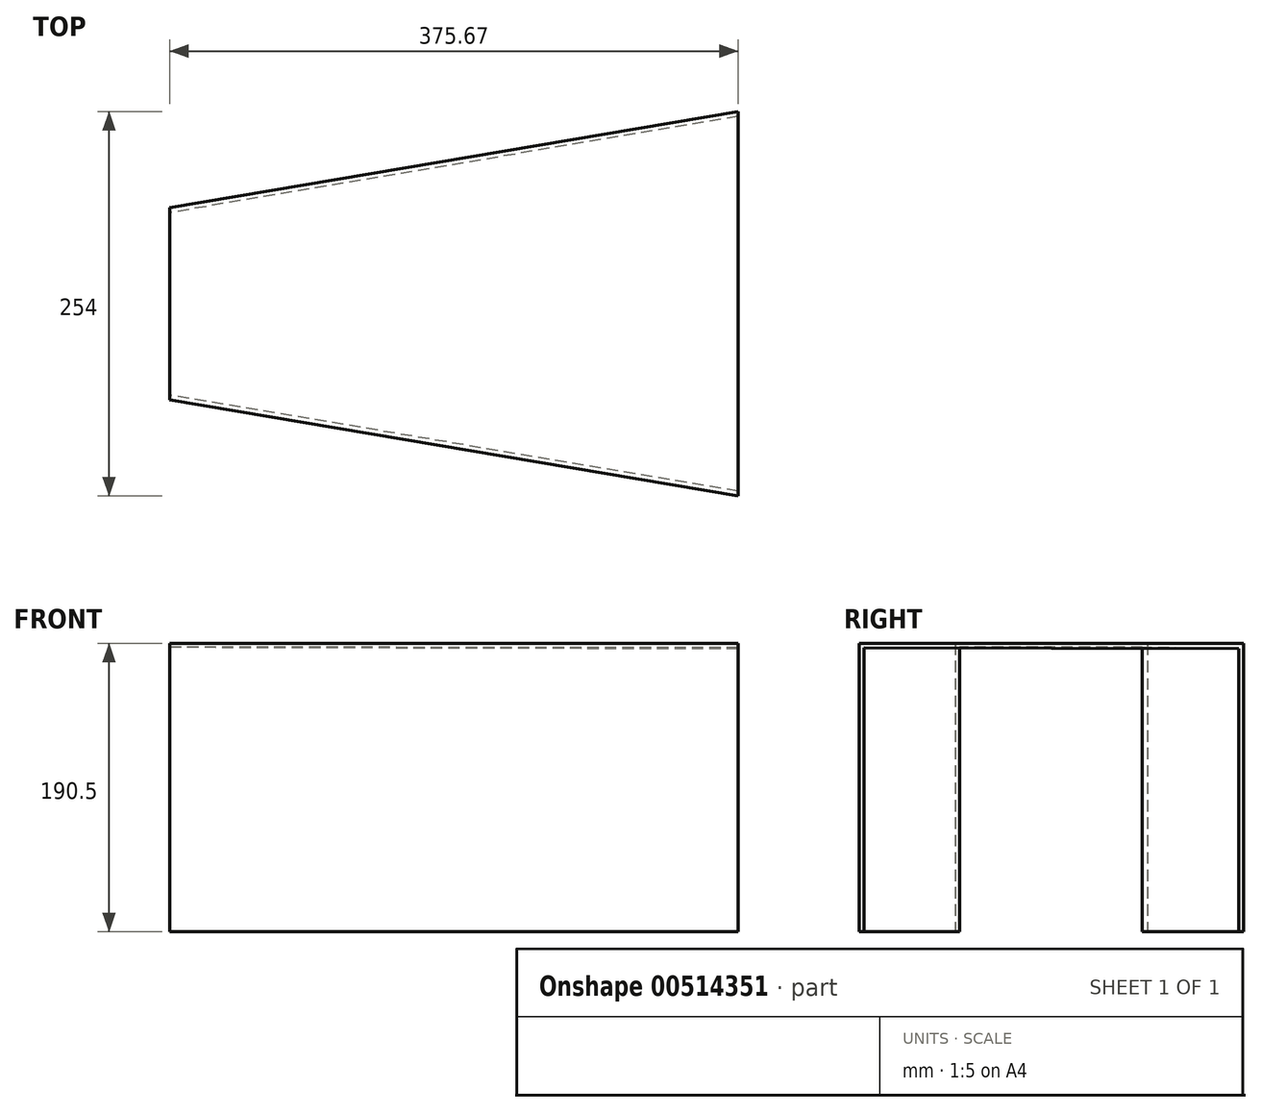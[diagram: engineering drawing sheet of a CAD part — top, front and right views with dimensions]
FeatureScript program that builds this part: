
annotation { "Feature Type Name" : "Feature", "Feature Type Description" : "" }
export const myFeature = defineFeature(function(context is Context, id is Id, definition is map)
    precondition{}
    {
        {
            var Q0;
            Q0=qCreatedBy(makeId("Top.planeOp"),FACE);
            var sketch = newSketch(context, id + "F0", { "sketchPlane" : qUnion([Q0])});
            skLineSegment(sketch, "E0", {"start": v(173.84, 75.91) * mm, "end": v(173.84, -178.09) * mm});
            skLineSegment(sketch, "E1", {"start": v(173.84, -178.09) * mm, "end": v(-201.83, -114.59) * mm});
            skLineSegment(sketch, "E2", {"start": v(-201.83, -114.59) * mm, "end": v(-201.83, 12.41) * mm});
            skLineSegment(sketch, "E3", {"start": v(-201.83, 12.41) * mm, "end": v(173.84, 75.91) * mm});
            skSolve(sketch);
        }
        {
            var Q0;
            Q0=makeQuery(id+"F0.imprint","IMPRINT",FACE,{"disambiguationData":[TD([[makeQuery(id+"F0.imprint","IMPRINT",EDGE,{"derivedFrom":sQuery(id+"F0.wireOp",EDGE,"E0")}),-1.0]])]});
            extrude(context, id + "F1", {"entities" : qUnion([Q0]), "depth" : 190.5 * mm});
        }
        {
            var Q0;
            Q0=makeQuery(id+"F1.opExtrude","SWEPT_FACE",FACE,{"disambiguationData":[OSD([sQuery(id+"F0.wireOp",EDGE,"E0")])]});
            var sketch = newSketch(context, id + "F2", { "sketchPlane" : qUnion([Q0])});
            skLineSegment(sketch, "E4", {"start": v(-174.85, 187.72) * mm, "end": v(-174.85, -9.13) * mm});
            skLineSegment(sketch, "E5", {"start": v(-174.85, -9.13) * mm, "end": v(72.8, -9.13) * mm});
            skLineSegment(sketch, "E6", {"start": v(72.8, -9.13) * mm, "end": v(72.8, 186.9) * mm});
            skLineSegment(sketch, "E7", {"start": v(72.8, 186.9) * mm, "end": v(-174.85, 187.72) * mm});
            skSolve(sketch);
        }
        {
            var Q0;
            Q0=makeQuery(id+"F1.opExtrude","SWEPT_FACE",FACE,{"disambiguationData":[OSD([sQuery(id+"F0.wireOp",EDGE,"E2")])]});
            var sketch = newSketch(context, id + "F3", { "sketchPlane" : qUnion([Q0])});
            skLineSegment(sketch, "E8", {"start": v(-9.08, 187.89) * mm, "end": v(111.57, 187.89) * mm});
            skLineSegment(sketch, "E9", {"start": v(111.57, 187.89) * mm, "end": v(111.57, -9.8) * mm});
            skLineSegment(sketch, "E10", {"start": v(111.57, -9.8) * mm, "end": v(-9.08, -9.8) * mm});
            skLineSegment(sketch, "E11", {"start": v(-9.08, -9.8) * mm, "end": v(-9.08, 187.89) * mm});
            skSolve(sketch);
        }
        {
            var Q1;
            {var subQ0=sQuery(id+"F2.wireOp",EDGE,"E7");Q1=makeQuery(id+"F2.imprint","IMPRINT",FACE,{"disambiguationData":[TD([[makeQuery(id+"F2.imprint","IMPRINT",EDGE,{"derivedFrom":subQ0}),1.0]])]});}
            var Q2;
            {var subQ0=sQuery(id+"F3.wireOp",EDGE,"E8");Q2=makeQuery(id+"F3.imprint","IMPRINT",FACE,{"disambiguationData":[TD([[makeQuery(id+"F3.imprint","IMPRINT",EDGE,{"derivedFrom":subQ0}),-1.0]])]});}
            loft(context, id + "F4", {"operationType" : NewBodyOperationType.REMOVE, "sheetProfilesArray" : [{ "sheetProfileEntities" : qUnion([Q1]) }, { "sheetProfileEntities" : qUnion([Q2]) }]});
        }
    });
